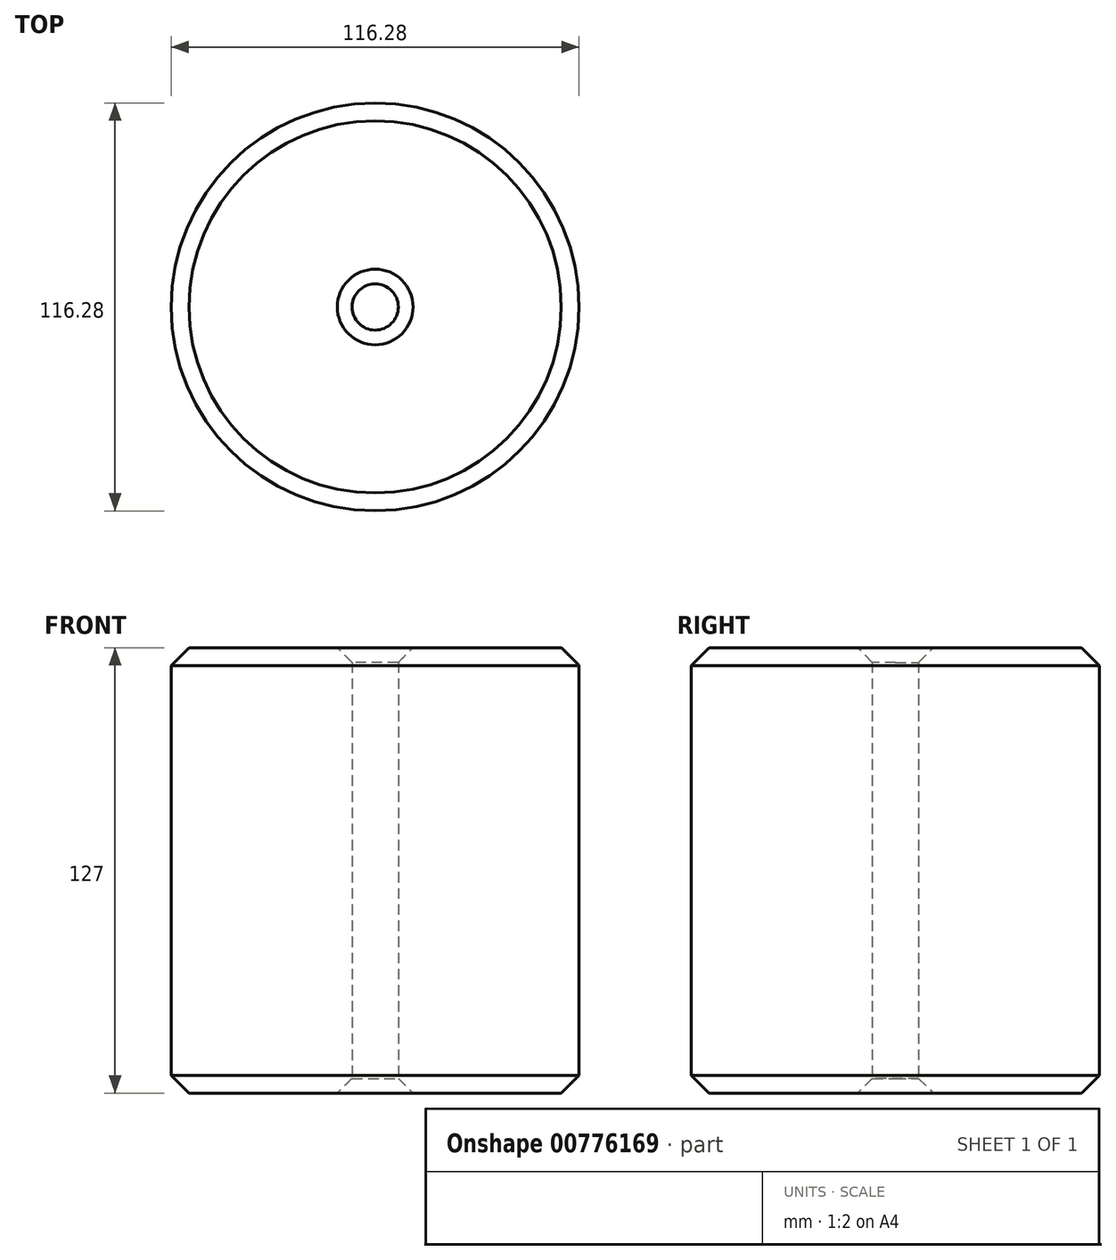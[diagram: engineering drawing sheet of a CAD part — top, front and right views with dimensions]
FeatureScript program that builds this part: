
annotation { "Feature Type Name" : "Feature", "Feature Type Description" : "" }
export const myFeature = defineFeature(function(context is Context, id is Id, definition is map)
    precondition{}
    {
        {
            var Q0;
            Q0=qCreatedBy(makeId("Top.planeOp"),FACE);
            var sketch = newSketch(context, id + "F0", { "sketchPlane" : qUnion([Q0])});
            skCircle(sketch, "E0", {"center": v(0, 0) * mm, "radius": 58.14 * mm});
            skCircle(sketch, "E1", {"center": v(0, 0) * mm, "radius": 5.7 * mm});
            skSolve(sketch);
        }
        {
            var Q0;
            Q0 = qSketchRegion(id + "F0", true);
            extrude(context, id + "F1", {"entities" : qUnion([Q0]), "depth" : 127 * mm, "offsetDistance" : 25.4 * mm});
        }
        {
            var Q0;
            Q0=makeQuery(id+"F1.opExtrude","CAP_FACE",FACE,{"disambiguationData":[OSD([sQuery(id+"F0.wireOp",EDGE,"E0")])],"isStart":false});
            chamfer(context, id + "F2", {"entities" : qUnion([Q0]), "width" : 5.08 * mm, "tangentPropagation" : true});
        }
        {
            var Q0;
            Q0=makeQuery(id+"F1.opExtrude","CAP_FACE",FACE,{"disambiguationData":[OSD([sQuery(id+"F0.wireOp",EDGE,"E0")])],"isStart":true});
            chamfer(context, id + "F3", {"entities" : qUnion([Q0]), "width" : 5.08 * mm, "tangentPropagation" : true});
        }
        {
            var Q0;
            Q0=sQuery(id+"F0.wireOp",VERTEX,"E0.center");
            var Q1;
            Q1=makeQuery(id+"F1.opExtrude","SWEPT_BODY",BODY,{"disambiguationData":[OSD([sQuery(id+"F0.wireOp",EDGE,"E0"),sQuery(id+"F0.wireOp",EDGE,"E1")])]});
            hole(context, id + "F4", {"style" : HoleStyle.SIMPLE, "endStyle" : HoleEndStyle.THROUGH, "oppositeDirection" : true, "standardTappedOrClearance" : lookupTablePath({ "standard" : "ISO", "fit" : "Normal", "size" : "M12", "type" : "Clearance" }), "standardBlindInLast" : lookupTablePath({ "fit" : "Standard", "standard" : "ISO", "size" : "M12", "type" : "Clearance" }), "holeDiameter" : 13.2 * mm, "majorDiameter" : 6.35 * mm, "isTappedThrough" : true, "tappedDepth" : 12.7 * mm, "tapClearance" : 3, "locations" : qUnion([Q0]), "scope" : qUnion([Q1])});
        }
    });
